# Revit family: Food-Service-Equipment_Oscartek_I3Dp1500-45H_cat
name_source: partatom
category: Specialty Equipment
units: mm (PartAtom-declared; Revit-internal decimal feet)

## family parameters
Always vertical = Yes
Classification Number = 23.40.40.11
Cut with Voids When Loaded = No
Enable Cutting in Views = No
Maintain Annotation Orientation = No
Part Type = Normal
Room Calculation Point = No
Round Connector Dimension = Use Diameter
Shared = No
Work Plane-Based = No

## types (1)
- Food-Service-Equipment_Oscartek_I3Dp1500-45H_cat
    Apparent Power = 612 VA
    Building Codes = https://www.arcat.com
    CSI Master Format = Foodservice Shelving
    CSI MasterFormat = 11 41 33
    Conn Conduit = Yes
    Construction Details = http://www.oscartek.com
    Cycle = 60 Hz
    Default Elevation = 0 "
    Description = ITALIA 1 DELI/PASTRY SHOWCASES
    FL Amps = 5 A
    Green Building-LEED = https://www.arcat.com
    Height = 45.26 "
    Installation-Fabrication = http://www.oscartek.com
    Length = 59 "
    Manufacturer = OSCARTEK
    Manufacturer Fax = 650-342-7400
    Manufacturer Website = http://www.oscartek.com
    Max Overcurrent Protection = 0 A
    Min Ckt Ampacity = 0 A
    Model = I3DP1500 45H
    Phase = 1
    Product Data = http://www.oscartek.com
    Revision = R1_2018-10
    Sales Information = http://www.oscartek.com
    Specification = https://www.arcat.com
    Test Data = http://www.oscartek.com
    Type Comments = As Specified
    URL = www.oscartek.com
    URL Cutsheet = www.oscartek.com
    Volts = 120 V
    Watts = 900 W
    Weight in Pounds = 352
    Width = 31 "

## geometry (parser evidence)
native form markers: Blend x22, Sweep x4
no freeform markers — native parametric forms only
